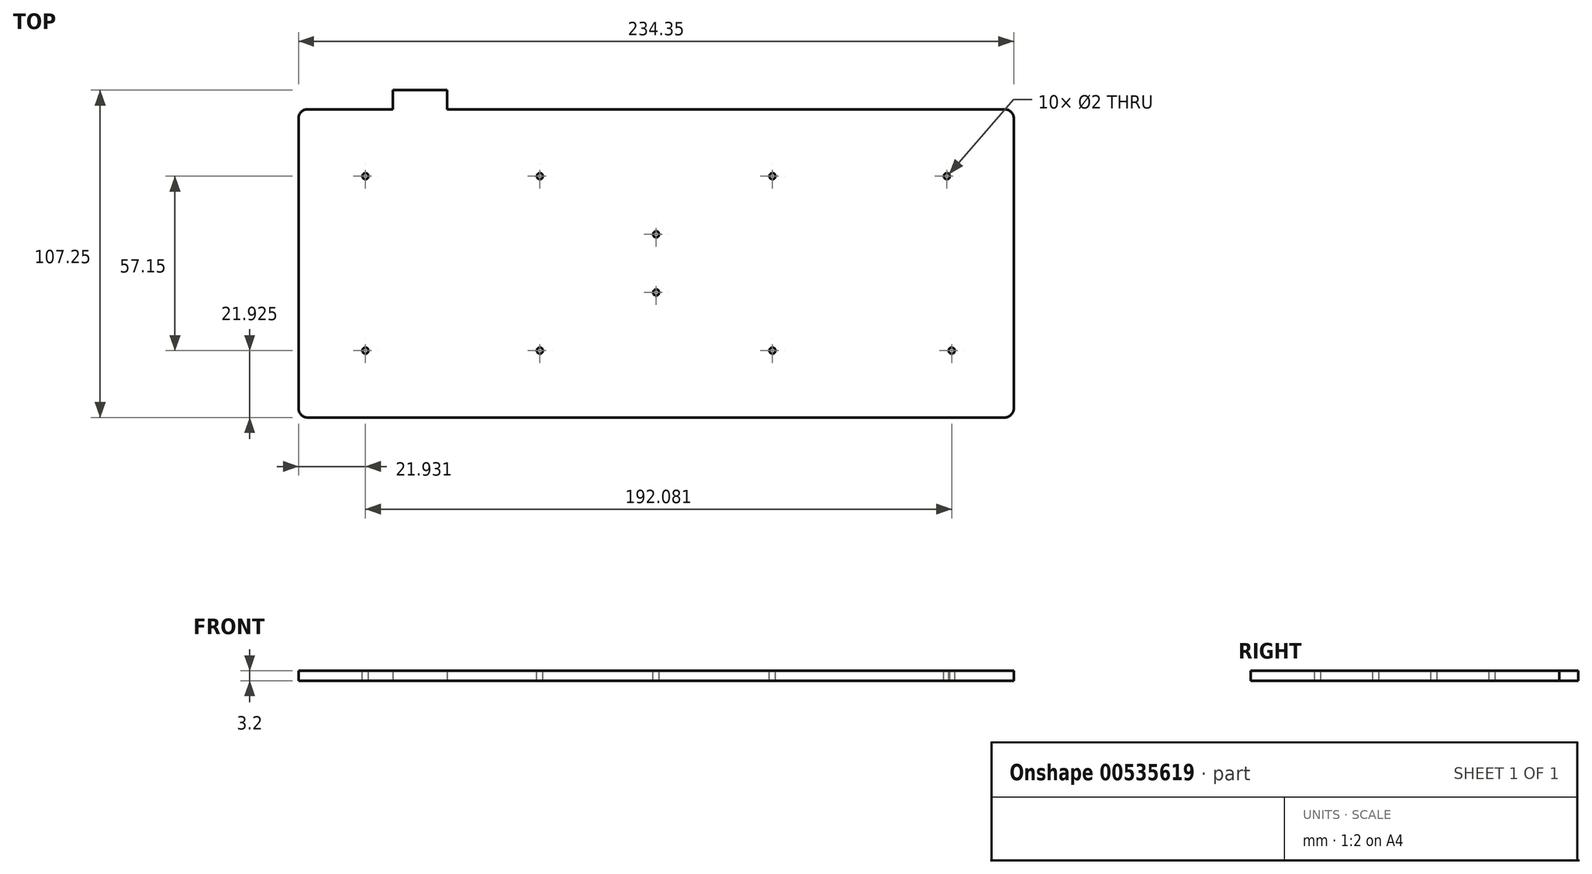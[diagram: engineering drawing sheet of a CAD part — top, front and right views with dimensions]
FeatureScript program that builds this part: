
annotation { "Feature Type Name" : "Feature", "Feature Type Description" : "" }
export const myFeature = defineFeature(function(context is Context, id is Id, definition is map)
    precondition{}
    {
        {
            var Q0;
            Q0=qCreatedBy(makeId("Top.planeOp"),FACE);
            var sketch = newSketch(context, id + "F0", { "sketchPlane" : qUnion([Q0])});
            skLineSegment(sketch, "E0", {"start": v(-117.17, 47.5) * mm, "end": v(-117.17, -47.5) * mm});
            skLineSegment(sketch, "E1", {"start": v(-114.17, -50.5) * mm, "end": v(114.17, -50.5) * mm});
            skLineSegment(sketch, "E2", {"start": v(117.17, -47.5) * mm, "end": v(117.18, 47.5) * mm});
            skLineSegment(sketch, "E3", {"start": v(114.18, 50.5) * mm, "end": v(-68.53, 50.5) * mm});
            skLineSegment(sketch, "E4", {"start": v(-68.53, 50.5) * mm, "end": v(-68.53, 56.75) * mm});
            skLineSegment(sketch, "E5", {"start": v(-68.53, 56.75) * mm, "end": v(-86.31, 56.75) * mm});
            skLineSegment(sketch, "E6", {"start": v(-86.31, 56.75) * mm, "end": v(-86.31, 50.5) * mm});
            skLineSegment(sketch, "E7", {"start": v(-86.31, 50.5) * mm, "end": v(-114.17, 50.5) * mm});
            skPoint(sketch, "E8.visualSharp", {"position": v(-117.17, 50.5) * mm});
            skArc(sketch, "E8.filletArc", {"start": v(-114.17, 50.5) * mm, "mid": v(-116.3, 49.62) * mm, "end": v(-117.17, 47.5) * mm});
            skPoint(sketch, "E9.visualSharp", {"position": v(-117.17, -50.5) * mm});
            skArc(sketch, "E9.filletArc", {"start": v(-117.17, -47.5) * mm, "mid": v(-116.3, -49.62) * mm, "end": v(-114.17, -50.5) * mm});
            skPoint(sketch, "E10.visualSharp", {"position": v(117.17, -50.5) * mm});
            skArc(sketch, "E10.filletArc", {"start": v(114.17, -50.5) * mm, "mid": v(116.3, -49.62) * mm, "end": v(117.17, -47.5) * mm});
            skPoint(sketch, "E11.visualSharp", {"position": v(117.18, 50.5) * mm});
            skArc(sketch, "E11.filletArc", {"start": v(117.18, 47.5) * mm, "mid": v(116.3, 49.62) * mm, "end": v(114.18, 50.5) * mm});
            skLineSegment(sketch, "E12", {"start": v(-117.18, 50.5) * mm, "end": v(0, 0) * mm});
            skLineSegment(sketch, "E13", {"start": v(0, 0) * mm, "end": v(117.17, -50.5) * mm});
            skSolve(sketch);
        }
        {
            var Q0;
            Q0 = qSketchRegion(id + "F0", true);
            extrude(context, id + "F1", {"entities" : qUnion([Q0]), "depth" : 3.2 * mm, "offsetDistance" : 25 * mm});
        }
        {
            var Q0;
            Q0=makeQuery(id+"F1.opExtrude","CAP_FACE",FACE,{"disambiguationData":[OSD([sQuery(id+"F0.wireOp",EDGE,"E0"),sQuery(id+"F0.wireOp",EDGE,"E1"),sQuery(id+"F0.wireOp",EDGE,"E2"),sQuery(id+"F0.wireOp",EDGE,"E3"),sQuery(id+"F0.wireOp",EDGE,"E4"),sQuery(id+"F0.wireOp",EDGE,"E5"),sQuery(id+"F0.wireOp",EDGE,"E6"),sQuery(id+"F0.wireOp",EDGE,"E7"),sQuery(id+"F0.wireOp",EDGE,"E8.filletArc"),sQuery(id+"F0.wireOp",EDGE,"E9.filletArc"),sQuery(id+"F0.wireOp",EDGE,"E10.filletArc"),sQuery(id+"F0.wireOp",EDGE,"E11.filletArc")])],"isStart":false});
            var sketch = newSketch(context, id + "F2", { "sketchPlane" : qUnion([Q0])});
            skCircle(sketch, "E14", {"center": v(96.83, -28.58) * mm, "radius": 1 * mm});
            skCircle(sketch, "E15", {"center": v(95.25, 28.58) * mm, "radius": 1 * mm});
            skCircle(sketch, "E16", {"center": v(38.1, -28.58) * mm, "radius": 1 * mm});
            skCircle(sketch, "E17", {"center": v(38.1, 28.58) * mm, "radius": 1 * mm});
            skCircle(sketch, "E18", {"center": v(0, -9.52) * mm, "radius": 1 * mm});
            skCircle(sketch, "E19", {"center": v(0, 9.52) * mm, "radius": 1 * mm});
            skCircle(sketch, "E20", {"center": v(-38.1, 28.58) * mm, "radius": 1 * mm});
            skCircle(sketch, "E21", {"center": v(-38.1, -28.58) * mm, "radius": 1 * mm});
            skCircle(sketch, "E22", {"center": v(-95.25, -28.58) * mm, "radius": 1 * mm});
            skCircle(sketch, "E23", {"center": v(-95.25, 28.58) * mm, "radius": 1 * mm});
            skLineSegment(sketch, "E24", {"start": v(-38.1, -28.58) * mm, "end": v(0, -9.52) * mm});
            skLineSegment(sketch, "E25", {"start": v(0, -9.52) * mm, "end": v(38.1, -28.58) * mm});
            skLineSegment(sketch, "E26", {"start": v(-38.1, 28.58) * mm, "end": v(0, 9.52) * mm});
            skLineSegment(sketch, "E27", {"start": v(0, 9.52) * mm, "end": v(38.1, 28.58) * mm});
            skLineSegment(sketch, "E28", {"start": v(0, 9.52) * mm, "end": v(0, 0) * mm});
            skLineSegment(sketch, "E29", {"start": v(0, -9.52) * mm, "end": v(0, 0) * mm});
            skSolve(sketch);
        }
        {
            var Q0;
            Q0 = qSketchRegion(id + "F2", true);
            extrude(context, id + "F3", {"entities" : qUnion([Q0]), "operationType" : NewBodyOperationType.REMOVE, "oppositeDirection" : true, "depth" : 3.2 * mm, "offsetDistance" : 25 * mm});
        }
    });
